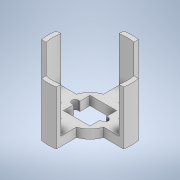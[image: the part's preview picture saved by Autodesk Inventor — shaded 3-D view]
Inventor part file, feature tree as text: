
AUTODESK INVENTOR PART (.ipt)
format: ipt  version: 2020 (Build 240168000, 168)  size: 207,360 bytes
history: native  units: mm
features: extrude x3, sketch x2, other x1, projected_geometry x1
ambient origin geometry x8: Origin, YZ Plane, XZ Plane, XY Plane, X Axis, Y Axis, Z Axis, Center Point
bodies: Body1 (feature_tree)
feature tree (7):
  other  "Твердое тело1"
  sketch  "Эскиз1"
  extrude  "Выдавливание1"  Depth=17.8mm
  extrude  "Выдавливание2"  Depth=17.8mm
  extrude  "Выдавливание3"  Depth=1.8mm
  sketch  "Эскиз2"
  projected_geometry  "Спроецированная петля1"
